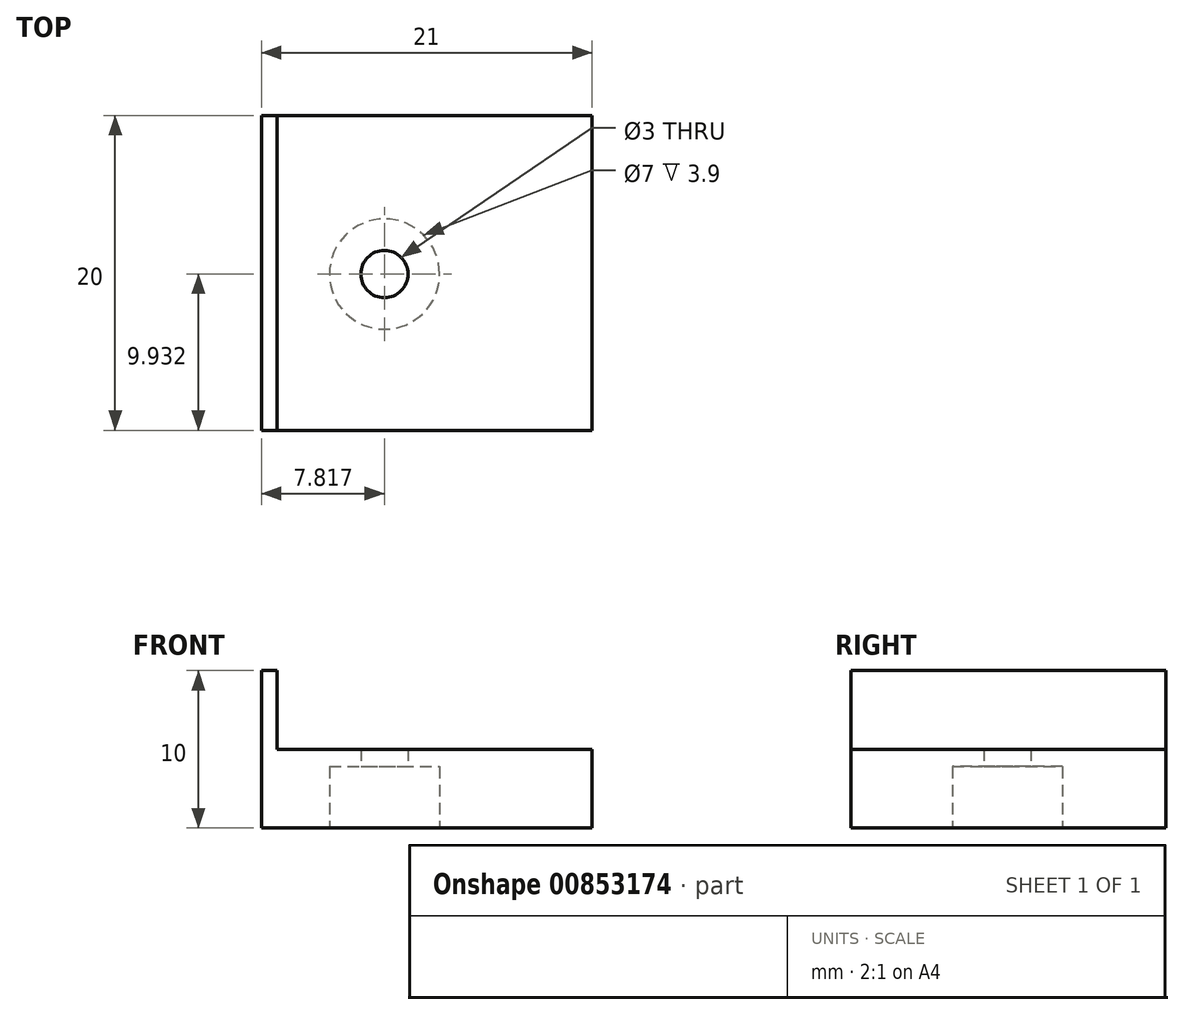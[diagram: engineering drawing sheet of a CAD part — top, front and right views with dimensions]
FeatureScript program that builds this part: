
annotation { "Feature Type Name" : "Feature", "Feature Type Description" : "" }
export const myFeature = defineFeature(function(context is Context, id is Id, definition is map)
    precondition{}
    {
        {
            var Q0;
            Q0=qCreatedBy(makeId("Top.planeOp"),FACE);
            var sketch = newSketch(context, id + "F0", { "sketchPlane" : qUnion([Q0])});
            skLineSegment(sketch, "E0.bottom", {"start": v(-28.37, 2.44) * mm, "end": v(-8.37, 2.44) * mm});
            skLineSegment(sketch, "E0.top", {"start": v(-28.37, -17.56) * mm, "end": v(-8.37, -17.56) * mm});
            skLineSegment(sketch, "E0.left", {"start": v(-28.37, 2.44) * mm, "end": v(-28.37, -17.56) * mm});
            skLineSegment(sketch, "E0.right", {"start": v(-8.37, 2.44) * mm, "end": v(-8.37, -17.56) * mm});
            skLineSegment(sketch, "E1", {"start": v(-28.37, 2.44) * mm, "end": v(-29.37, 2.44) * mm});
            skLineSegment(sketch, "E2", {"start": v(-28.37, -17.56) * mm, "end": v(-29.37, -17.56) * mm});
            skLineSegment(sketch, "E3", {"start": v(-29.37, -17.56) * mm, "end": v(-29.37, 2.44) * mm});
            skSolve(sketch);
        }
        {
            var Q0;
            Q0=makeQuery(id+"F0.imprint","IMPRINT",FACE,{"disambiguationData":[TD([[makeQuery(id+"F0.imprint","IMPRINT",EDGE,{"derivedFrom":sQuery(id+"F0.wireOp",EDGE,"E0.left")}),-1.0]])]});
            extrude(context, id + "F1", {"entities" : qUnion([Q0]), "depth" : 10 * mm, "offsetDistance" : 25 * mm});
        }
        {
            var Q0;
            Q0=makeQuery(id+"F0.imprint","IMPRINT",FACE,{"disambiguationData":[TD([[makeQuery(id+"F0.imprint","IMPRINT",EDGE,{"derivedFrom":sQuery(id+"F0.wireOp",EDGE,"E0.bottom")}),-1.0]])]});
            var Q1;
            Q1=makeQuery(id+"F0.imprint","IMPRINT",FACE,{"disambiguationData":[TD([[makeQuery(id+"F0.imprint","IMPRINT",EDGE,{"derivedFrom":sQuery(id+"F0.wireOp",EDGE,"E0.left")}),-1.0]])]});
            extrude(context, id + "F2", {"entities" : qUnion([Q0, Q1]), "operationType" : NewBodyOperationType.ADD, "depth" : 5 * mm, "offsetDistance" : 25 * mm});
        }
        {
            var Q0;
            Q0=qCreatedBy(makeId("Top.planeOp"),FACE);
            var sketch = newSketch(context, id + "F3", { "sketchPlane" : qUnion([Q0])});
            skCircle(sketch, "E4", {"center": v(-21.55, -7.63) * mm, "radius": 1.09 * mm});
            skCircle(sketch, "E5", {"center": v(-21.55, -7.63) * mm, "radius": 2.45 * mm});
            skSolve(sketch);
        }
        {
            var Q0;
            Q0=sQuery(id+"F3.wireOp",VERTEX,"E4.center");
            var Q1;
            Q1=makeQuery(id+"F1.opExtrude","SWEPT_BODY",BODY,{"disambiguationData":[OSD([sQuery(id+"F0.wireOp",EDGE,"E0.left"),sQuery(id+"F0.wireOp",EDGE,"E1"),sQuery(id+"F0.wireOp",EDGE,"E2"),sQuery(id+"F0.wireOp",EDGE,"E3")])]});
            hole(context, id + "F4", {"style" : HoleStyle.C_BORE, "endStyle" : HoleEndStyle.THROUGH, "oppositeDirection" : true, "holeDiameter" : 3 * mm, "cBoreDiameter" : 7 * mm, "cBoreDepth" : 3.9 * mm, "majorDiameter" : 5 * mm, "isTappedThrough" : true, "tappedDepth" : 12 * mm, "tapClearance" : 3, "locations" : qUnion([Q0]), "scope" : qUnion([Q1])});
        }
    });
